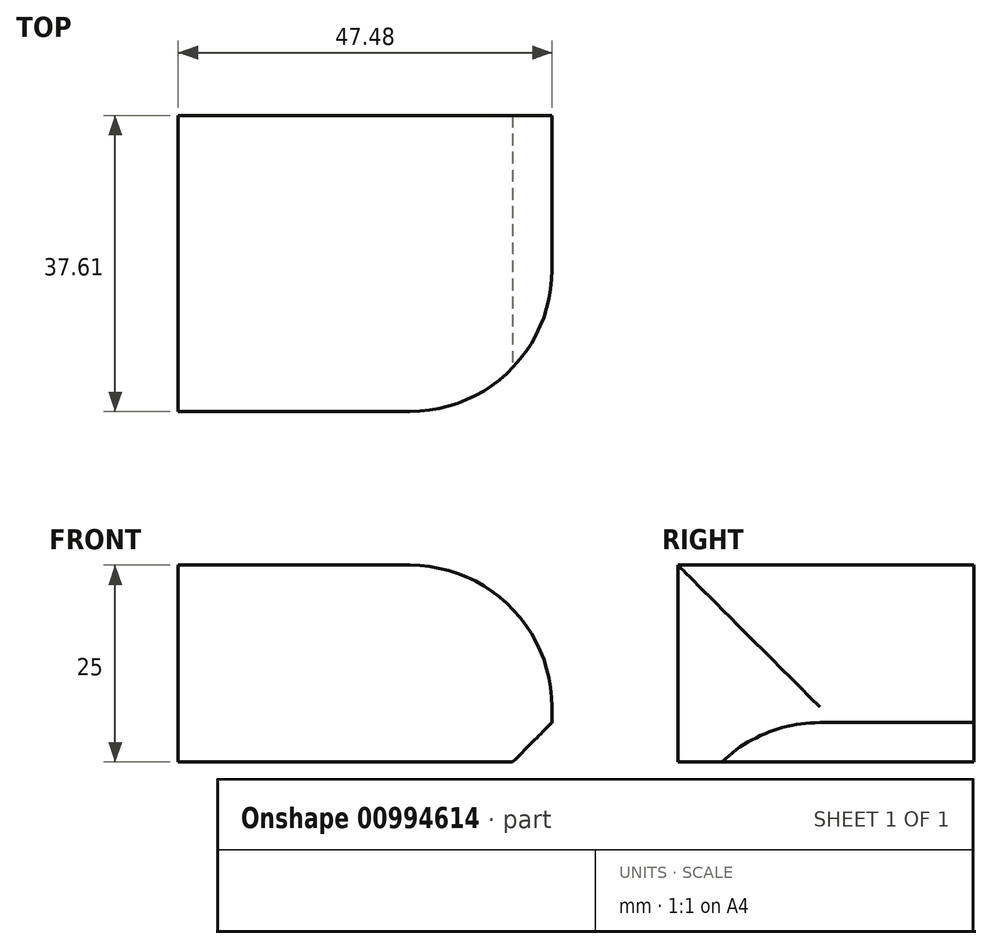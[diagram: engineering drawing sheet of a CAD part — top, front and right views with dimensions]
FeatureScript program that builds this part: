
annotation { "Feature Type Name" : "Feature", "Feature Type Description" : "" }
export const myFeature = defineFeature(function(context is Context, id is Id, definition is map)
    precondition{}
    {
        {
            var Q0;
            Q0=qCreatedBy(makeId("Top.planeOp"),FACE);
            var sketch = newSketch(context, id + "F0", { "sketchPlane" : qUnion([Q0])});
            skLineSegment(sketch, "E0.bottom", {"start": v(27.78, 0) * mm, "end": v(-19.7, 0) * mm});
            skLineSegment(sketch, "E0.top", {"start": v(27.78, -37.6) * mm, "end": v(-19.7, -37.6) * mm});
            skLineSegment(sketch, "E0.left", {"start": v(27.78, 0) * mm, "end": v(27.78, -37.6) * mm});
            skLineSegment(sketch, "E0.right", {"start": v(-19.7, 0) * mm, "end": v(-19.7, -37.6) * mm});
            skSolve(sketch);
        }
        {
            var Q0;
            Q0=qCreatedBy(makeId("Top.planeOp"),FACE);
            var sketch = newSketch(context, id + "F1", { "sketchPlane" : qUnion([Q0])});
            skCircle(sketch, "E1", {"center": v(68.24, 41.06) * mm, "radius": 36.16 * mm});
            skSolve(sketch);
        }
        {
            var Q0;
            Q0=makeQuery(id+"F0.imprint","IMPRINT",FACE,{"disambiguationData":[TD([[makeQuery(id+"F0.imprint","IMPRINT",EDGE,{"derivedFrom":sQuery(id+"F0.wireOp",EDGE,"E0.bottom")}),1.0]])]});
            extrude(context, id + "F2", {"entities" : qUnion([Q0]), "oppositeDirection" : true, "depth" : 25 * mm, "offsetDistance" : 25 * mm});
        }
        {
            var Q0;
            Q0=makeQuery(id+"F2.opExtrude","CAP_EDGE",EDGE,{"disambiguationData":[OSD([sQuery(id+"F0.wireOp",EDGE,"E0.left")])],"isStart":false});
            chamfer(context, id + "F3", {"entities" : qUnion([Q0]), "width" : 5 * mm, "tangentPropagation" : true});
        }
        {
            var Q0;
            Q0=makeQuery(id+"F2.opExtrude","CAP_EDGE",EDGE,{"disambiguationData":[OSD([sQuery(id+"F0.wireOp",EDGE,"E0.left")])],"isStart":true});
            var Q1;
            Q1=makeQuery(id+"F2.opExtrude","SWEPT_EDGE",EDGE,{"disambiguationData":[OSD([sQuery(id+"F0.wireOp",EDGE,"E0.top"),sQuery(id+"F0.wireOp",EDGE,"E0.left")])]});
            fillet(context, id + "F4", {"entities" : qUnion([Q0, Q1]), "radius" : 18.01 * mm, "tangentPropagation" : true, "allowEdgeOverflow" : false});
        }
    });
